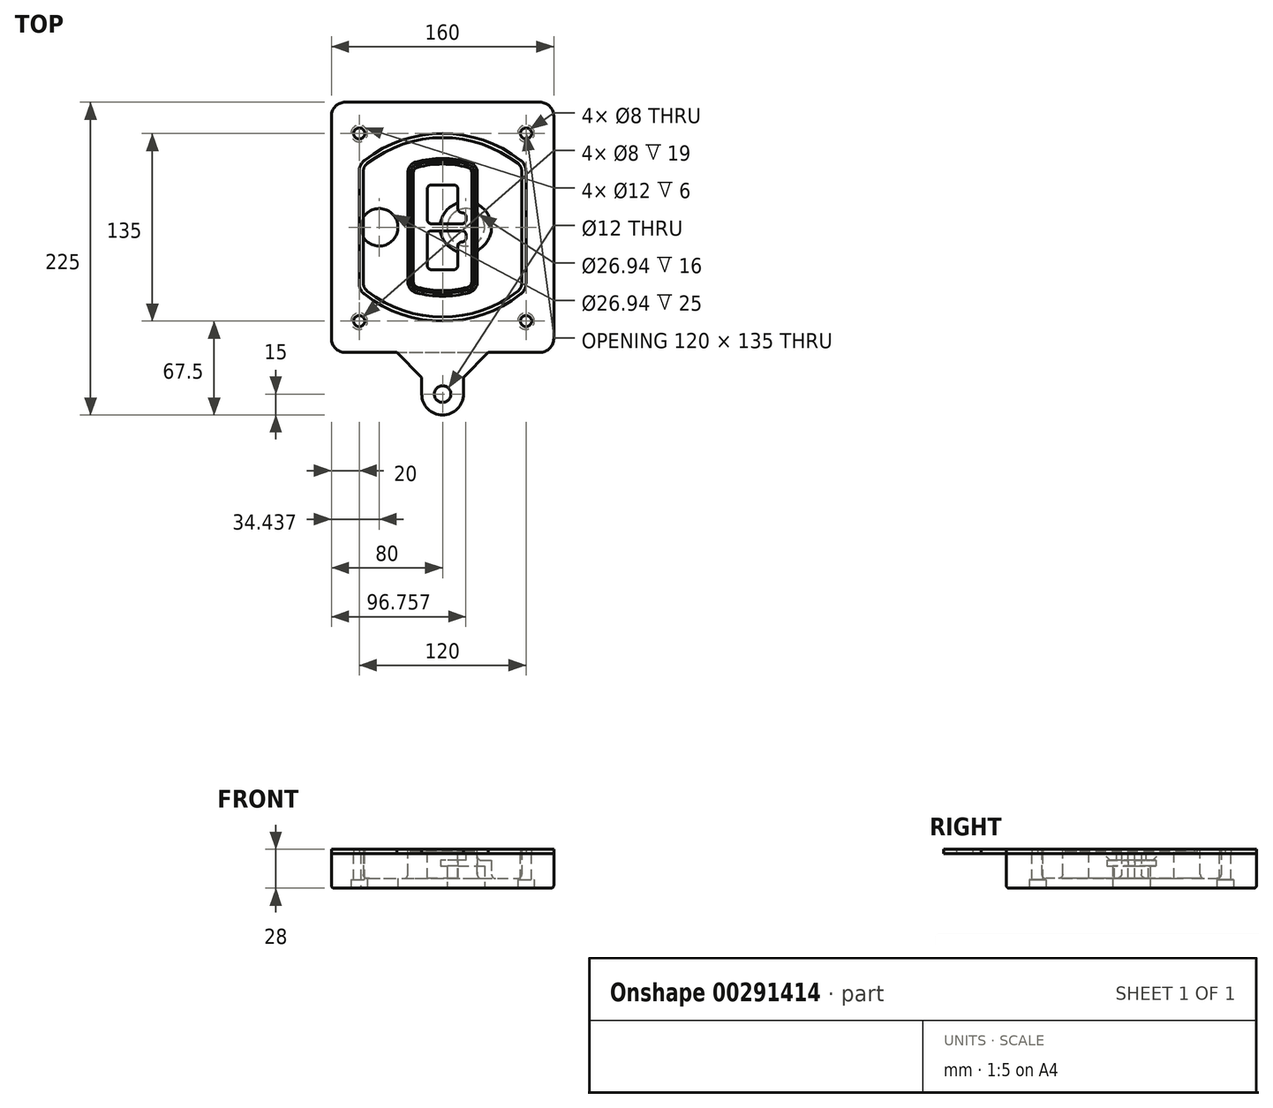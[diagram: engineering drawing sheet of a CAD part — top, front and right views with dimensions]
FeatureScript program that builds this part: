
annotation { "Feature Type Name" : "Feature", "Feature Type Description" : "" }
export const myFeature = defineFeature(function(context is Context, id is Id, definition is map)
    precondition{}
    {
        {
            var Q0;
            Q0=qCreatedBy(makeId("Top.planeOp"),FACE);
            var sketch = newSketch(context, id + "F0", { "sketchPlane" : qUnion([Q0])});
            skPoint(sketch, "E0.rect.middle", {"position": v(0, 0) * mm});
            skLineSegment(sketch, "E1.bottom", {"start": v(-70, -90) * mm, "end": v(70, -90) * mm});
            skLineSegment(sketch, "E1.top", {"start": v(-70, 90) * mm, "end": v(70, 90) * mm});
            skLineSegment(sketch, "E1.left", {"start": v(-80, -80) * mm, "end": v(-80, 80) * mm});
            skLineSegment(sketch, "E1.right", {"start": v(80, -80) * mm, "end": v(80, 80) * mm});
            skLineSegment(sketch, "E2", {"start": v(-80, 90) * mm, "end": v(80, -90) * mm, "construction": true});
            skLineSegment(sketch, "E3", {"start": v(80, 90) * mm, "end": v(-80, -90) * mm, "construction": true});
            skCircle(sketch, "E4", {"center": v(-60, 67.5) * mm, "radius": 4 * mm});
            skCircle(sketch, "E5", {"center": v(60, 67.5) * mm, "radius": 4 * mm});
            skCircle(sketch, "E6", {"center": v(60, -67.5) * mm, "radius": 4 * mm});
            skCircle(sketch, "E7", {"center": v(-60, -67.5) * mm, "radius": 4 * mm});
            skLineSegment(sketch, "E8", {"start": v(-60, 67.5) * mm, "end": v(60, 67.5) * mm, "construction": true});
            skLineSegment(sketch, "E9", {"start": v(60, 67.5) * mm, "end": v(60, -67.5) * mm, "construction": true});
            skLineSegment(sketch, "E10", {"start": v(60, -67.5) * mm, "end": v(-60, -67.5) * mm, "construction": true});
            skLineSegment(sketch, "E11", {"start": v(-60, -67.5) * mm, "end": v(-60, 67.5) * mm, "construction": true});
            skLineSegment(sketch, "E12", {"start": v(-60, 40.3) * mm, "end": v(-60, -40.3) * mm});
            skLineSegment(sketch, "E13", {"start": v(60, 40.3) * mm, "end": v(60, -40.3) * mm});
            skArc(sketch, "E14", {"start": v(56.15, 48.18) * mm, "mid": v(0, 67.5) * mm, "end": v(-56.15, 48.18) * mm});
            skArc(sketch, "E15", {"start": v(-56.15, -48.18) * mm, "mid": v(0, -67.5) * mm, "end": v(56.15, -48.18) * mm});
            skLineSegment(sketch, "E16", {"start": v(-60, 0) * mm, "end": v(60, 0) * mm, "construction": true});
            skPoint(sketch, "E17.visualSharp", {"position": v(-60, -45) * mm});
            skArc(sketch, "E17.filletArc", {"start": v(-60, -40.3) * mm, "mid": v(-58.99, -44.68) * mm, "end": v(-56.15, -48.18) * mm});
            skPoint(sketch, "E18.visualSharp", {"position": v(-60, 45) * mm});
            skArc(sketch, "E18.filletArc", {"start": v(-56.15, 48.18) * mm, "mid": v(-58.99, 44.68) * mm, "end": v(-60, 40.3) * mm});
            skPoint(sketch, "E19.visualSharp", {"position": v(60, 45) * mm});
            skArc(sketch, "E19.filletArc", {"start": v(60, 40.3) * mm, "mid": v(58.99, 44.68) * mm, "end": v(56.15, 48.18) * mm});
            skPoint(sketch, "E20.visualSharp", {"position": v(60, -45) * mm});
            skArc(sketch, "E20.filletArc", {"start": v(56.15, -48.18) * mm, "mid": v(58.99, -44.68) * mm, "end": v(60, -40.3) * mm});
            skPoint(sketch, "E21.visualSharp", {"position": v(-80, 90) * mm});
            skArc(sketch, "E21.filletArc", {"start": v(-70, 90) * mm, "mid": v(-77.07, 87.07) * mm, "end": v(-80, 80) * mm});
            skPoint(sketch, "E22.visualSharp", {"position": v(80, 90) * mm});
            skArc(sketch, "E22.filletArc", {"start": v(80, 80) * mm, "mid": v(77.07, 87.07) * mm, "end": v(70, 90) * mm});
            skPoint(sketch, "E23.visualSharp", {"position": v(80, -90) * mm});
            skArc(sketch, "E23.filletArc", {"start": v(70, -90) * mm, "mid": v(77.07, -87.07) * mm, "end": v(80, -80) * mm});
            skPoint(sketch, "E24.visualSharp", {"position": v(-80, -90) * mm});
            skArc(sketch, "E24.filletArc", {"start": v(-80, -80) * mm, "mid": v(-77.07, -87.07) * mm, "end": v(-70, -90) * mm});
            skArc(sketch, "E25.0", {"start": v(57, 40.3) * mm, "mid": v(56.3, 43.36) * mm, "end": v(54.3, 45.81) * mm});
            skLineSegment(sketch, "E25.1", {"start": v(57, 40.3) * mm, "end": v(57, -40.3) * mm});
            skArc(sketch, "E25.2", {"start": v(54.3, -45.81) * mm, "mid": v(56.3, -43.36) * mm, "end": v(57, -40.3) * mm});
            skArc(sketch, "E25.3", {"start": v(-54.3, -45.81) * mm, "mid": v(0, -64.5) * mm, "end": v(54.3, -45.81) * mm});
            skArc(sketch, "E25.4", {"start": v(-57, -40.3) * mm, "mid": v(-56.3, -43.36) * mm, "end": v(-54.3, -45.81) * mm});
            skArc(sketch, "E25.5", {"start": v(54.3, 45.81) * mm, "mid": v(0, 64.5) * mm, "end": v(-54.3, 45.81) * mm});
            skLineSegment(sketch, "E25.6", {"start": v(-57, 40.3) * mm, "end": v(-57, -40.3) * mm});
            skArc(sketch, "E25.7", {"start": v(-54.3, 45.81) * mm, "mid": v(-56.3, 43.36) * mm, "end": v(-57, 40.3) * mm});
            skArc(sketch, "E26.0", {"start": v(-58.62, 51.33) * mm, "mid": v(-62.58, 46.43) * mm, "end": v(-64, 40.3) * mm});
            skArc(sketch, "E26.1", {"start": v(58.62, 51.33) * mm, "mid": v(0, 71.5) * mm, "end": v(-58.62, 51.33) * mm});
            skArc(sketch, "E26.2", {"start": v(64, 40.3) * mm, "mid": v(62.58, 46.43) * mm, "end": v(58.62, 51.33) * mm});
            skLineSegment(sketch, "E26.3", {"start": v(64, 40.3) * mm, "end": v(64, -40.3) * mm});
            skArc(sketch, "E26.4", {"start": v(58.62, -51.33) * mm, "mid": v(62.58, -46.43) * mm, "end": v(64, -40.3) * mm});
            skLineSegment(sketch, "E26.5", {"start": v(-64, 40.3) * mm, "end": v(-64, -40.3) * mm});
            skArc(sketch, "E26.6", {"start": v(-58.62, -51.33) * mm, "mid": v(0, -71.5) * mm, "end": v(58.62, -51.33) * mm});
            skArc(sketch, "E26.7", {"start": v(-64, -40.3) * mm, "mid": v(-62.58, -46.43) * mm, "end": v(-58.62, -51.33) * mm});
            skSolve(sketch);
        }
        {
            var Q0;
            Q0=makeQuery(id+"F0.imprint","IMPRINT",FACE,{"disambiguationData":[TD([[makeQuery(id+"F0.imprint","IMPRINT",EDGE,{"derivedFrom":sQuery(id+"F0.wireOp",EDGE,"E1.bottom")}),1.0]])]});
            var Q1;
            Q1=makeQuery(id+"F0.imprint","IMPRINT",FACE,{"disambiguationData":[TD([[makeQuery(id+"F0.imprint","IMPRINT",EDGE,{"derivedFrom":sQuery(id+"F0.wireOp",EDGE,"E12")}),1.0]])]});
            var Q2;
            Q2=makeQuery(id+"F0.imprint","IMPRINT",FACE,{"disambiguationData":[TD([[makeQuery(id+"F0.imprint","IMPRINT",EDGE,{"derivedFrom":sQuery(id+"F0.wireOp",EDGE,"E25.0")}),1.0]])]});
            var Q3;
            Q3=makeQuery(id+"F0.imprint","IMPRINT",FACE,{"disambiguationData":[TD([[makeQuery(id+"F0.imprint","IMPRINT",EDGE,{"derivedFrom":sQuery(id+"F0.wireOp",EDGE,"E12")}),-1.0]])]});
            extrude(context, id + "F1", {"entities" : qUnion([Q0, Q1, Q2, Q3]), "oppositeDirection" : true, "depth" : 25 * mm});
        }
        {
            var Q0;
            Q0=makeQuery(id+"F0.imprint","IMPRINT",FACE,{"disambiguationData":[TD([[makeQuery(id+"F0.imprint","IMPRINT",EDGE,{"derivedFrom":sQuery(id+"F0.wireOp",EDGE,"E12")}),1.0]])]});
            extrude(context, id + "F2", {"entities" : qUnion([Q0]), "operationType" : NewBodyOperationType.ADD, "depth" : 3 * mm});
        }
        {
            var Q0;
            Q0=makeQuery(id+"F0.imprint","IMPRINT",FACE,{"disambiguationData":[TD([[makeQuery(id+"F0.imprint","IMPRINT",EDGE,{"derivedFrom":sQuery(id+"F0.wireOp",EDGE,"E25.0")}),1.0]])]});
            extrude(context, id + "F3", {"entities" : qUnion([Q0]), "operationType" : NewBodyOperationType.REMOVE, "oppositeDirection" : true, "depth" : 18 * mm});
        }
        {
            var Q0;
            Q0=makeQuery(id+"F2.opExtrude","CAP_FACE",FACE,{"disambiguationData":[OSD([sQuery(id+"F0.wireOp",EDGE,"E12"),sQuery(id+"F0.wireOp",EDGE,"E13"),sQuery(id+"F0.wireOp",EDGE,"E14"),sQuery(id+"F0.wireOp",EDGE,"E15"),sQuery(id+"F0.wireOp",EDGE,"E17.filletArc"),sQuery(id+"F0.wireOp",EDGE,"E18.filletArc"),sQuery(id+"F0.wireOp",EDGE,"E19.filletArc"),sQuery(id+"F0.wireOp",EDGE,"E20.filletArc"),sQuery(id+"F0.wireOp",EDGE,"E25.0"),sQuery(id+"F0.wireOp",EDGE,"E25.1"),sQuery(id+"F0.wireOp",EDGE,"E25.2"),sQuery(id+"F0.wireOp",EDGE,"E25.3"),sQuery(id+"F0.wireOp",EDGE,"E25.4"),sQuery(id+"F0.wireOp",EDGE,"E25.5"),sQuery(id+"F0.wireOp",EDGE,"E25.6"),sQuery(id+"F0.wireOp",EDGE,"E25.7")])],"isStart":false});
            var sketch = newSketch(context, id + "F4", { "sketchPlane" : qUnion([Q0])});
            skArc(sketch, "E27.0", {"start": v(-19.08, -46.97) * mm, "mid": v(0, -49.5) * mm, "end": v(19.08, -46.97) * mm});
            skArc(sketch, "E28.0", {"start": v(19.08, 46.97) * mm, "mid": v(0, 49.5) * mm, "end": v(-19.08, 46.97) * mm});
            skLineSegment(sketch, "E29", {"start": v(-25, 39.25) * mm, "end": v(-25, -39.25) * mm});
            skLineSegment(sketch, "E30", {"start": v(25, 39.25) * mm, "end": v(25, -39.25) * mm});
            skLineSegment(sketch, "E31", {"start": v(-25, 45.1) * mm, "end": v(25, 45.1) * mm, "construction": true});
            skLineSegment(sketch, "E32", {"start": v(-25, -45.1) * mm, "end": v(25, -45.1) * mm, "construction": true});
            skPoint(sketch, "E33.visualSharp", {"position": v(-25, 45.1) * mm});
            skArc(sketch, "E33.filletArc", {"start": v(-19.08, 46.97) * mm, "mid": v(-23.35, 44.11) * mm, "end": v(-25, 39.25) * mm});
            skPoint(sketch, "E34.visualSharp", {"position": v(25, 45.1) * mm});
            skArc(sketch, "E34.filletArc", {"start": v(25, 39.25) * mm, "mid": v(23.35, 44.11) * mm, "end": v(19.08, 46.97) * mm});
            skPoint(sketch, "E35.visualSharp", {"position": v(25, -45.1) * mm});
            skArc(sketch, "E35.filletArc", {"start": v(19.08, -46.97) * mm, "mid": v(23.35, -44.11) * mm, "end": v(25, -39.25) * mm});
            skPoint(sketch, "E36.visualSharp", {"position": v(-25, -45.1) * mm});
            skArc(sketch, "E36.filletArc", {"start": v(-25, -39.25) * mm, "mid": v(-23.35, -44.11) * mm, "end": v(-19.08, -46.97) * mm});
            skArc(sketch, "E37.0", {"start": v(54.3, 45.81) * mm, "mid": v(0, 64.5) * mm, "end": v(-54.3, 45.81) * mm});
            skArc(sketch, "E37.1", {"start": v(-54.3, 45.81) * mm, "mid": v(-56.3, 43.36) * mm, "end": v(-57, 40.3) * mm});
            skLineSegment(sketch, "E37.2", {"start": v(-57, 40.3) * mm, "end": v(-57, -40.3) * mm});
            skArc(sketch, "E37.3", {"start": v(-57, -40.3) * mm, "mid": v(-56.3, -43.36) * mm, "end": v(-54.3, -45.81) * mm});
            skArc(sketch, "E37.4", {"start": v(-54.3, -45.81) * mm, "mid": v(0, -64.5) * mm, "end": v(54.3, -45.81) * mm});
            skArc(sketch, "E37.5", {"start": v(54.3, -45.81) * mm, "mid": v(56.3, -43.36) * mm, "end": v(57, -40.3) * mm});
            skLineSegment(sketch, "E37.6", {"start": v(57, 40.3) * mm, "end": v(57, -40.3) * mm});
            skArc(sketch, "E37.7", {"start": v(57, 40.3) * mm, "mid": v(56.3, 43.36) * mm, "end": v(54.3, 45.81) * mm});
            skLineSegment(sketch, "E38.0", {"start": v(23, 39.25) * mm, "end": v(23, -39.25) * mm});
            skArc(sketch, "E38.1", {"start": v(18.56, -45.04) * mm, "mid": v(21.76, -42.9) * mm, "end": v(23, -39.25) * mm});
            skArc(sketch, "E38.2", {"start": v(-18.56, -45.04) * mm, "mid": v(0, -47.5) * mm, "end": v(18.56, -45.04) * mm});
            skArc(sketch, "E38.3", {"start": v(-23, -39.25) * mm, "mid": v(-21.76, -42.9) * mm, "end": v(-18.56, -45.04) * mm});
            skLineSegment(sketch, "E38.4", {"start": v(-23, 39.25) * mm, "end": v(-23, -39.25) * mm});
            skArc(sketch, "E38.5", {"start": v(23, 39.25) * mm, "mid": v(21.76, 42.9) * mm, "end": v(18.56, 45.04) * mm});
            skArc(sketch, "E38.6", {"start": v(-18.56, 45.04) * mm, "mid": v(-21.76, 42.9) * mm, "end": v(-23, 39.25) * mm});
            skArc(sketch, "E38.7", {"start": v(18.56, 45.04) * mm, "mid": v(0, 47.5) * mm, "end": v(-18.56, 45.04) * mm});
            skArc(sketch, "E39.0", {"start": v(21, 39.25) * mm, "mid": v(20.18, 41.68) * mm, "end": v(18.04, 43.1) * mm});
            skLineSegment(sketch, "E39.1", {"start": v(21, 39.25) * mm, "end": v(21, -39.25) * mm});
            skArc(sketch, "E39.2", {"start": v(18.04, -43.1) * mm, "mid": v(20.18, -41.68) * mm, "end": v(21, -39.25) * mm});
            skArc(sketch, "E39.3", {"start": v(-18.04, -43.1) * mm, "mid": v(0, -45.5) * mm, "end": v(18.04, -43.1) * mm});
            skArc(sketch, "E39.4", {"start": v(-21, -39.25) * mm, "mid": v(-20.18, -41.68) * mm, "end": v(-18.04, -43.1) * mm});
            skArc(sketch, "E39.5", {"start": v(18.04, 43.1) * mm, "mid": v(0, 45.5) * mm, "end": v(-18.04, 43.1) * mm});
            skLineSegment(sketch, "E39.6", {"start": v(-21, 39.25) * mm, "end": v(-21, -39.25) * mm});
            skArc(sketch, "E39.7", {"start": v(-18.04, 43.1) * mm, "mid": v(-20.18, 41.68) * mm, "end": v(-21, 39.25) * mm});
            skLineSegment(sketch, "E40", {"start": v(-25, 0) * mm, "end": v(25, 0) * mm, "construction": true});
            skLineSegment(sketch, "E41", {"start": v(-11, 5.5) * mm, "end": v(-11, 27.5) * mm});
            skLineSegment(sketch, "E42", {"start": v(-8, 30.5) * mm, "end": v(8, 30.5) * mm});
            skLineSegment(sketch, "E43", {"start": v(11, 27.5) * mm, "end": v(11, 13.5) * mm});
            skLineSegment(sketch, "E44", {"start": v(14, 10.5) * mm, "end": v(14, 10.5) * mm});
            skLineSegment(sketch, "E45", {"start": v(17, 7.5) * mm, "end": v(17, 5.5) * mm});
            skLineSegment(sketch, "E46", {"start": v(14, 2.5) * mm, "end": v(-8, 2.5) * mm});
            skPoint(sketch, "E47.visualSharp", {"position": v(-11, 30.5) * mm});
            skArc(sketch, "E47.filletArc", {"start": v(-8, 30.5) * mm, "mid": v(-10.12, 29.62) * mm, "end": v(-11, 27.5) * mm});
            skPoint(sketch, "E48.visualSharp", {"position": v(11, 30.5) * mm});
            skArc(sketch, "E48.filletArc", {"start": v(11, 27.5) * mm, "mid": v(10.12, 29.62) * mm, "end": v(8, 30.5) * mm});
            skPoint(sketch, "E49.visualSharp", {"position": v(11, 10.5) * mm});
            skArc(sketch, "E49.filletArc", {"start": v(11, 13.5) * mm, "mid": v(11.88, 11.38) * mm, "end": v(14, 10.5) * mm});
            skPoint(sketch, "E50.visualSharp", {"position": v(17, 10.5) * mm});
            skArc(sketch, "E50.filletArc", {"start": v(17, 7.5) * mm, "mid": v(16.12, 9.62) * mm, "end": v(14, 10.5) * mm});
            skPoint(sketch, "E51.visualSharp", {"position": v(17, 2.5) * mm});
            skArc(sketch, "E51.filletArc", {"start": v(14, 2.5) * mm, "mid": v(16.12, 3.38) * mm, "end": v(17, 5.5) * mm});
            skPoint(sketch, "E52.visualSharp", {"position": v(-11, 2.5) * mm});
            skArc(sketch, "E52.filletArc", {"start": v(-11, 5.5) * mm, "mid": v(-10.12, 3.38) * mm, "end": v(-8, 2.5) * mm});
            skLineSegment(sketch, "E53.0.MirrorCS", {"start": v(14, -2.5) * mm, "end": v(-8, -2.5) * mm});
            skArc(sketch, "E54.0.MirrorCS", {"start": v(-11, -5.5) * mm, "mid": v(-10.12, -3.38) * mm, "end": v(-8, -2.5) * mm});
            skLineSegment(sketch, "E55.0.MirrorCS", {"start": v(-11, -5.5) * mm, "end": v(-11, -27.5) * mm});
            skArc(sketch, "E56.0.MirrorCS", {"start": v(-8, -30.5) * mm, "mid": v(-10.12, -29.62) * mm, "end": v(-11, -27.5) * mm});
            skLineSegment(sketch, "E57.0.MirrorCS", {"start": v(-8, -30.5) * mm, "end": v(8, -30.5) * mm});
            skArc(sketch, "E58.0.MirrorCS", {"start": v(11, -27.5) * mm, "mid": v(10.12, -29.62) * mm, "end": v(8, -30.5) * mm});
            skLineSegment(sketch, "E59.0.MirrorCS", {"start": v(11, -27.5) * mm, "end": v(11, -13.5) * mm});
            skArc(sketch, "E60.0.MirrorCS", {"start": v(11, -13.5) * mm, "mid": v(11.88, -11.38) * mm, "end": v(14, -10.5) * mm});
            skArc(sketch, "E61.0.MirrorCS", {"start": v(17, -7.5) * mm, "mid": v(16.12, -9.62) * mm, "end": v(14, -10.5) * mm});
            skLineSegment(sketch, "E62.0.MirrorCS", {"start": v(17, -7.5) * mm, "end": v(17, -5.5) * mm});
            skArc(sketch, "E63.0.MirrorCS", {"start": v(14, -2.5) * mm, "mid": v(16.12, -3.38) * mm, "end": v(17, -5.5) * mm});
            skSolve(sketch);
        }
        {
            var Q0;
            Q0=makeQuery(id+"F4.imprint","IMPRINT",FACE,{"disambiguationData":[TD([[makeQuery(id+"F4.imprint","IMPRINT",EDGE,{"derivedFrom":sQuery(id+"F4.wireOp",EDGE,"E27.0")}),1.0]])]});
            var Q1;
            Q1=makeQuery(id+"F4.imprint","IMPRINT",FACE,{"disambiguationData":[TD([[makeQuery(id+"F4.imprint","IMPRINT",EDGE,{"derivedFrom":sQuery(id+"F4.wireOp",EDGE,"E38.0")}),-1.0]])]});
            var Q2;
            Q2=makeQuery(id+"F4.imprint","IMPRINT",FACE,{"disambiguationData":[TD([[makeQuery(id+"F4.imprint","IMPRINT",EDGE,{"derivedFrom":sQuery(id+"F4.wireOp",EDGE,"E39.0")}),1.0]])]});
            extrude(context, id + "F5", {"entities" : qUnion([Q0, Q1, Q2]), "operationType" : NewBodyOperationType.ADD, "endBound" : BoundingType.UP_TO_NEXT, "oppositeDirection" : true, "depth" : 25 * mm});
        }
        {
            var Q0;
            Q0=makeQuery(id+"F4.imprint","IMPRINT",FACE,{"disambiguationData":[TD([[makeQuery(id+"F4.imprint","IMPRINT",EDGE,{"derivedFrom":sQuery(id+"F4.wireOp",EDGE,"E38.0")}),-1.0]])]});
            extrude(context, id + "F6", {"entities" : qUnion([Q0]), "operationType" : NewBodyOperationType.REMOVE, "oppositeDirection" : true, "depth" : 2 * mm});
        }
        {
            var Q0;
            Q0=makeQuery(id+"F1.opExtrude","CAP_FACE",FACE,{"disambiguationData":[OSD([sQuery(id+"F0.wireOp",EDGE,"E1.bottom"),sQuery(id+"F0.wireOp",EDGE,"E1.top"),sQuery(id+"F0.wireOp",EDGE,"E1.left"),sQuery(id+"F0.wireOp",EDGE,"E1.right"),sQuery(id+"F0.wireOp",EDGE,"E4"),sQuery(id+"F0.wireOp",EDGE,"E5"),sQuery(id+"F0.wireOp",EDGE,"E6"),sQuery(id+"F0.wireOp",EDGE,"E7"),sQuery(id+"F0.wireOp",EDGE,"E21.filletArc"),sQuery(id+"F0.wireOp",EDGE,"E22.filletArc"),sQuery(id+"F0.wireOp",EDGE,"E23.filletArc"),sQuery(id+"F0.wireOp",EDGE,"E24.filletArc")])],"isStart":false});
            var sketch = newSketch(context, id + "F7", { "sketchPlane" : qUnion([Q0])});
            skCircle(sketch, "E64", {"center": v(16.76, 0) * mm, "radius": 13.47 * mm});
            skCircle(sketch, "E65", {"center": v(-45.56, 0) * mm, "radius": 13.47 * mm});
            skLineSegment(sketch, "E66", {"start": v(80, 0) * mm, "end": v(-80, 0) * mm});
            skCircle(sketch, "E67", {"center": v(16.76, 0) * mm, "radius": 18.47 * mm});
            skCircle(sketch, "E68", {"center": v(60, -67.5) * mm, "radius": 6 * mm});
            skCircle(sketch, "E69", {"center": v(-60, -67.5) * mm, "radius": 6 * mm});
            skCircle(sketch, "E70", {"center": v(-60, 67.5) * mm, "radius": 6 * mm});
            skCircle(sketch, "E71", {"center": v(60, 67.5) * mm, "radius": 6 * mm});
            skSolve(sketch);
        }
        {
            var Q0;
            {var subQ1=sQuery(id+"F7.wireOp",EDGE,"E66");var subQ4=sQuery(id+"F7.wireOp",EDGE,"E64");var subQ6=makeQuery(id+"F7.imprint","INTERSECT",VERTEX,{"disambiguationData":[OD(0.0)],"derivedFrom":[subQ4,subQ1]});Q0=makeQuery(id+"F7.imprint","IMPRINT",FACE,{"disambiguationData":[TD([[makeQuery(id+"F7.imprint","IMPRINT",EDGE,{"disambiguationData":[TD([[subQ6,-1.0]])],"derivedFrom":subQ4}),-1.0]])]});}
            var Q1;
            {var subQ0=sQuery(id+"F7.wireOp",EDGE,"E66");var subQ1=sQuery(id+"F7.wireOp",EDGE,"E64");var subQ3=makeQuery(id+"F7.imprint","INTERSECT",VERTEX,{"disambiguationData":[OD(0.0)],"derivedFrom":[subQ1,subQ0]});Q1=makeQuery(id+"F7.imprint","IMPRINT",FACE,{"disambiguationData":[TD([[makeQuery(id+"F7.imprint","IMPRINT",EDGE,{"disambiguationData":[TD([[subQ3,-1.0]])],"derivedFrom":subQ1}),1.0]])]});}
            var Q2;
            {var subQ0=sQuery(id+"F7.wireOp",EDGE,"E66");var subQ1=sQuery(id+"F7.wireOp",EDGE,"E64");var subQ3=makeQuery(id+"F7.imprint","INTERSECT",VERTEX,{"disambiguationData":[OD(0.0)],"derivedFrom":[subQ1,subQ0]});Q2=makeQuery(id+"F7.imprint","IMPRINT",FACE,{"disambiguationData":[TD([[makeQuery(id+"F7.imprint","IMPRINT",EDGE,{"disambiguationData":[TD([[subQ3,1.0]])],"derivedFrom":subQ1}),1.0]])]});}
            var Q3;
            {var subQ1=sQuery(id+"F7.wireOp",EDGE,"E66");var subQ4=sQuery(id+"F7.wireOp",EDGE,"E64");var subQ6=makeQuery(id+"F7.imprint","INTERSECT",VERTEX,{"disambiguationData":[OD(0.0)],"derivedFrom":[subQ4,subQ1]});Q3=makeQuery(id+"F7.imprint","IMPRINT",FACE,{"disambiguationData":[TD([[makeQuery(id+"F7.imprint","IMPRINT",EDGE,{"disambiguationData":[TD([[subQ6,1.0]])],"derivedFrom":subQ4}),-1.0]])]});}
            extrude(context, id + "F8", {"entities" : qUnion([Q0, Q1, Q2, Q3]), "operationType" : NewBodyOperationType.ADD, "oppositeDirection" : true, "depth" : 20 * mm});
        }
        {
            var Q0;
            {var subQ0=sQuery(id+"F7.wireOp",EDGE,"E66");var subQ1=sQuery(id+"F7.wireOp",EDGE,"E64");var subQ3=makeQuery(id+"F7.imprint","INTERSECT",VERTEX,{"disambiguationData":[OD(0.0)],"derivedFrom":[subQ1,subQ0]});Q0=makeQuery(id+"F7.imprint","IMPRINT",FACE,{"disambiguationData":[TD([[makeQuery(id+"F7.imprint","IMPRINT",EDGE,{"disambiguationData":[TD([[subQ3,-1.0]])],"derivedFrom":subQ1}),1.0]])]});}
            var Q1;
            {var subQ0=sQuery(id+"F7.wireOp",EDGE,"E66");var subQ1=sQuery(id+"F7.wireOp",EDGE,"E64");var subQ3=makeQuery(id+"F7.imprint","INTERSECT",VERTEX,{"disambiguationData":[OD(0.0)],"derivedFrom":[subQ1,subQ0]});Q1=makeQuery(id+"F7.imprint","IMPRINT",FACE,{"disambiguationData":[TD([[makeQuery(id+"F7.imprint","IMPRINT",EDGE,{"disambiguationData":[TD([[subQ3,1.0]])],"derivedFrom":subQ1}),1.0]])]});}
            extrude(context, id + "F9", {"entities" : qUnion([Q0, Q1]), "operationType" : NewBodyOperationType.REMOVE, "oppositeDirection" : true, "depth" : 16 * mm});
        }
        {
            var Q0;
            {var subQ0=sQuery(id+"F7.wireOp",EDGE,"E66");var subQ1=sQuery(id+"F7.wireOp",EDGE,"E65");var subQ3=makeQuery(id+"F7.imprint","INTERSECT",VERTEX,{"disambiguationData":[OD(0.0)],"derivedFrom":[subQ1,subQ0]});Q0=makeQuery(id+"F7.imprint","IMPRINT",FACE,{"disambiguationData":[TD([[makeQuery(id+"F7.imprint","IMPRINT",EDGE,{"disambiguationData":[TD([[subQ3,-1.0]])],"derivedFrom":subQ1}),1.0]])]});}
            var Q1;
            {var subQ0=sQuery(id+"F7.wireOp",EDGE,"E66");var subQ1=sQuery(id+"F7.wireOp",EDGE,"E65");var subQ3=makeQuery(id+"F7.imprint","INTERSECT",VERTEX,{"disambiguationData":[OD(0.0)],"derivedFrom":[subQ1,subQ0]});Q1=makeQuery(id+"F7.imprint","IMPRINT",FACE,{"disambiguationData":[TD([[makeQuery(id+"F7.imprint","IMPRINT",EDGE,{"disambiguationData":[TD([[subQ3,1.0]])],"derivedFrom":subQ1}),1.0]])]});}
            extrude(context, id + "F10", {"entities" : qUnion([Q0, Q1]), "operationType" : NewBodyOperationType.REMOVE, "oppositeDirection" : true, "depth" : 25 * mm});
        }
        {
            var Q0;
            Q0=makeQuery(id+"F7.imprint","IMPRINT",FACE,{"disambiguationData":[TD([[makeQuery(id+"F7.imprint","IMPRINT",EDGE,{"derivedFrom":sQuery(id+"F7.wireOp",EDGE,"E68")}),1.0]])]});
            var Q1;
            Q1=makeQuery(id+"F7.imprint","IMPRINT",FACE,{"disambiguationData":[TD([[makeQuery(id+"F7.imprint","IMPRINT",EDGE,{"derivedFrom":makeQuery(id+"F1.opExtrude","CAP_EDGE",EDGE,{"disambiguationData":[OSD([sQuery(id+"F0.wireOp",EDGE,"E5")])],"isStart":false})}),-1.0]])]});
            var Q2;
            Q2=makeQuery(id+"F7.imprint","IMPRINT",FACE,{"disambiguationData":[TD([[makeQuery(id+"F7.imprint","IMPRINT",EDGE,{"derivedFrom":sQuery(id+"F7.wireOp",EDGE,"E69")}),1.0]])]});
            var Q3;
            Q3=makeQuery(id+"F7.imprint","IMPRINT",FACE,{"disambiguationData":[TD([[makeQuery(id+"F7.imprint","IMPRINT",EDGE,{"derivedFrom":makeQuery(id+"F1.opExtrude","CAP_EDGE",EDGE,{"disambiguationData":[OSD([sQuery(id+"F0.wireOp",EDGE,"E4")])],"isStart":false})}),-1.0]])]});
            var Q4;
            Q4=makeQuery(id+"F7.imprint","IMPRINT",FACE,{"disambiguationData":[TD([[makeQuery(id+"F7.imprint","IMPRINT",EDGE,{"derivedFrom":sQuery(id+"F7.wireOp",EDGE,"E70")}),1.0]])]});
            var Q5;
            Q5=makeQuery(id+"F7.imprint","IMPRINT",FACE,{"disambiguationData":[TD([[makeQuery(id+"F7.imprint","IMPRINT",EDGE,{"derivedFrom":makeQuery(id+"F1.opExtrude","CAP_EDGE",EDGE,{"disambiguationData":[OSD([sQuery(id+"F0.wireOp",EDGE,"E7")])],"isStart":false})}),-1.0]])]});
            var Q6;
            Q6=makeQuery(id+"F7.imprint","IMPRINT",FACE,{"disambiguationData":[TD([[makeQuery(id+"F7.imprint","IMPRINT",EDGE,{"derivedFrom":sQuery(id+"F7.wireOp",EDGE,"E71")}),1.0]])]});
            var Q7;
            Q7=makeQuery(id+"F7.imprint","IMPRINT",FACE,{"disambiguationData":[TD([[makeQuery(id+"F7.imprint","IMPRINT",EDGE,{"derivedFrom":makeQuery(id+"F1.opExtrude","CAP_EDGE",EDGE,{"disambiguationData":[OSD([sQuery(id+"F0.wireOp",EDGE,"E6")])],"isStart":false})}),-1.0]])]});
            extrude(context, id + "F11", {"entities" : qUnion([Q0, Q1, Q2, Q3, Q4, Q5, Q6, Q7]), "operationType" : NewBodyOperationType.REMOVE, "oppositeDirection" : true, "depth" : 6 * mm});
        }
        {
            var Q0;
            Q0=makeQuery(id+"F9.boolean.opBoolean","COPY",FACE,{"derivedFrom":makeQuery(id+"F9.opExtrude","CAP_FACE",FACE,{"disambiguationData":[OSD([sQuery(id+"F7.wireOp",EDGE,"E64")])],"isStart":false})});
            var sketch = newSketch(context, id + "F12", { "sketchPlane" : qUnion([Q0])});
            skArc(sketch, "E72.0", {"start": v(11, 17.55) * mm, "mid": v(2.57, 11.82) * mm, "end": v(-1.54, 2.5) * mm});
            skArc(sketch, "E72.1", {"start": v(-1.54, -2.5) * mm, "mid": v(2.57, -11.82) * mm, "end": v(11, -17.55) * mm});
            skLineSegment(sketch, "E73", {"start": v(-1.54, -2.5) * mm, "end": v(14, -2.5) * mm});
            skLineSegment(sketch, "E74.0", {"start": v(14, 2.5) * mm, "end": v(-1.54, 2.5) * mm});
            skArc(sketch, "E74.1", {"start": v(14, 2.5) * mm, "mid": v(16.12, 3.38) * mm, "end": v(17, 5.5) * mm});
            skLineSegment(sketch, "E74.2", {"start": v(17, 7.5) * mm, "end": v(17, 5.5) * mm});
            skArc(sketch, "E74.3", {"start": v(17, 7.5) * mm, "mid": v(16.12, 9.62) * mm, "end": v(14, 10.5) * mm});
            skArc(sketch, "E74.4", {"start": v(11, 13.5) * mm, "mid": v(11.88, 11.38) * mm, "end": v(14, 10.5) * mm});
            skLineSegment(sketch, "E74.5", {"start": v(11, 17.55) * mm, "end": v(11, 13.5) * mm});
            skLineSegment(sketch, "E74.7", {"start": v(14, -2.5) * mm, "end": v(-1.54, -2.5) * mm});
            skArc(sketch, "E74.8", {"start": v(14, -2.5) * mm, "mid": v(16.12, -3.38) * mm, "end": v(17, -5.5) * mm});
            skLineSegment(sketch, "E74.9", {"start": v(17, -7.5) * mm, "end": v(17, -5.5) * mm});
            skArc(sketch, "E74.10", {"start": v(17, -7.5) * mm, "mid": v(16.12, -9.62) * mm, "end": v(14, -10.5) * mm});
            skArc(sketch, "E74.11", {"start": v(11, -13.5) * mm, "mid": v(11.88, -11.38) * mm, "end": v(14, -10.5) * mm});
            skLineSegment(sketch, "E74.12", {"start": v(11, -17.55) * mm, "end": v(11, -13.5) * mm});
            skPoint(sketch, "E75.orphan", {"position": v(11, -27.5) * mm});
            skPoint(sketch, "E76.orphan", {"position": v(-8, -2.5) * mm});
            skPoint(sketch, "E77.orphan", {"position": v(-8, 2.5) * mm});
            skPoint(sketch, "E78.orphan", {"position": v(11, 27.5) * mm});
            skSolve(sketch);
        }
        {
            var Q0;
            {var subQ7=sQuery(id+"F12.wireOp",EDGE,"E72.0");var subQ14=sQuery(id+"F12.wireOp",EDGE,"E72.1");var subQ16=sQuery(id+"F12.wireOp",EDGE,"E74.1");var subQ18=sQuery(id+"F12.wireOp",EDGE,"E74.8");Q0=qUnion([makeQuery(id+"F12.imprint","IMPRINT",FACE,{"disambiguationData":[TD([[makeQuery(id+"F12.imprint","IMPRINT",EDGE,{"derivedFrom":subQ7}),1.0]])]}),makeQuery(id+"F12.imprint","IMPRINT",FACE,{"disambiguationData":[TD([[makeQuery(id+"F12.imprint","IMPRINT",EDGE,{"derivedFrom":subQ14}),1.0]])]}),makeQuery(id+"F12.imprint","IMPRINT",FACE,{"disambiguationData":[TD([[makeQuery(id+"F12.imprint","IMPRINT",EDGE,{"derivedFrom":subQ16}),1.0]])]}),makeQuery(id+"F12.imprint","IMPRINT",FACE,{"disambiguationData":[TD([[makeQuery(id+"F12.imprint","IMPRINT",EDGE,{"derivedFrom":subQ18}),-1.0]])]})]);}
            var Q1;
            Q1=makeQuery(id+"F5.boolean.opBoolean","SPLIT",FACE,{"disambiguationData":[TD([makeQuery(id+"F5.opExtrude","SWEPT_FACE",FACE,{"disambiguationData":[OSD([sQuery(id+"F4.wireOp",EDGE,"E41")])]})])],"derivedFrom":makeQuery(id+"F3.boolean.opBoolean","COPY",FACE,{"derivedFrom":makeQuery(id+"F3.opExtrude","CAP_FACE",FACE,{"disambiguationData":[OSD([sQuery(id+"F0.wireOp",EDGE,"E25.0"),sQuery(id+"F0.wireOp",EDGE,"E25.1"),sQuery(id+"F0.wireOp",EDGE,"E25.2"),sQuery(id+"F0.wireOp",EDGE,"E25.3"),sQuery(id+"F0.wireOp",EDGE,"E25.4"),sQuery(id+"F0.wireOp",EDGE,"E25.5"),sQuery(id+"F0.wireOp",EDGE,"E25.6"),sQuery(id+"F0.wireOp",EDGE,"E25.7")])],"isStart":false})})});
            extrude(context, id + "F13", {"entities" : qUnion([Q0]), "operationType" : NewBodyOperationType.REMOVE, "endBound" : BoundingType.UP_TO_SURFACE, "endBoundEntityFace" : qUnion([Q1]), "depth" : 25 * mm});
        }
        {
            var Q0;
            Q0=makeQuery(id+"F3.boolean.opBoolean","COPY",EDGE,{"derivedFrom":makeQuery(id+"F3.opExtrude","CAP_EDGE",EDGE,{"disambiguationData":[OSD([sQuery(id+"F0.wireOp",EDGE,"E25.6")])],"isStart":false})});
            var Q1;
            Q1=makeQuery(id+"F8.boolean.opBoolean","INTERSECT",EDGE,{"derivedFrom":[makeQuery(id+"F5.opExtrude","SWEPT_FACE",FACE,{"disambiguationData":[OSD([sQuery(id+"F4.wireOp",EDGE,"E30")])]}),makeQuery(id+"F8.opExtrude","CAP_FACE",FACE,{"disambiguationData":[OSD([sQuery(id+"F7.wireOp",EDGE,"E67")])],"isStart":false})]});
            var Q2;
            Q2=makeQuery(id+"F8.boolean.opBoolean","INTERSECT",EDGE,{"disambiguationData":[OD(1.0)],"derivedFrom":[makeQuery(id+"F5.opExtrude","SWEPT_FACE",FACE,{"disambiguationData":[OSD([sQuery(id+"F4.wireOp",EDGE,"E30")])]}),makeQuery(id+"F8.opExtrude","SWEPT_FACE",FACE,{"disambiguationData":[OSD([sQuery(id+"F7.wireOp",EDGE,"E67")])]})]});
            var Q3;
            {var subQ0=sQuery(id+"F4.wireOp",EDGE,"E30");Q3=makeQuery(id+"F8.boolean.opBoolean","SPLIT",EDGE,{"disambiguationData":[TD([makeQuery(id+"F5.opExtrude","SWEPT_FACE",FACE,{"disambiguationData":[OSD([sQuery(id+"F4.wireOp",EDGE,"E35.filletArc")])]})])],"derivedFrom":makeQuery(id+"F5.opExtrude","CAP_EDGE",EDGE,{"disambiguationData":[OSD([subQ0])],"isStart":false})});}
            var Q4;
            {var subQ0=sQuery(id+"F0.wireOp",EDGE,"E25.7");var subQ1=sQuery(id+"F0.wireOp",EDGE,"E25.1");var subQ2=sQuery(id+"F0.wireOp",EDGE,"E25.6");var subQ3=sQuery(id+"F0.wireOp",EDGE,"E25.5");var subQ4=sQuery(id+"F0.wireOp",EDGE,"E25.4");var subQ5=sQuery(id+"F0.wireOp",EDGE,"E25.0");var subQ6=sQuery(id+"F0.wireOp",EDGE,"E25.2");var subQ7=sQuery(id+"F0.wireOp",EDGE,"E25.3");Q4=makeQuery(id+"F8.boolean.opBoolean","INTERSECT",EDGE,{"derivedFrom":[makeQuery(id+"F5.boolean.opBoolean","SPLIT",FACE,{"disambiguationData":[TD([makeQuery(id+"F2.opExtrude","SWEPT_FACE",FACE,{"disambiguationData":[OSD([subQ5])]})])],"derivedFrom":makeQuery(id+"F3.boolean.opBoolean","COPY",FACE,{"derivedFrom":makeQuery(id+"F3.opExtrude","CAP_FACE",FACE,{"disambiguationData":[OSD([subQ5,subQ1,subQ6,subQ7,subQ4,subQ3,subQ2,subQ0])],"isStart":false})})}),makeQuery(id+"F8.opExtrude","SWEPT_FACE",FACE,{"disambiguationData":[OSD([sQuery(id+"F7.wireOp",EDGE,"E67")])]})]});}
            var Q5;
            Q5=makeQuery(id+"F8.boolean.opBoolean","INTERSECT",EDGE,{"disambiguationData":[OD(0.0)],"derivedFrom":[makeQuery(id+"F5.opExtrude","SWEPT_FACE",FACE,{"disambiguationData":[OSD([sQuery(id+"F4.wireOp",EDGE,"E30")])]}),makeQuery(id+"F8.opExtrude","SWEPT_FACE",FACE,{"disambiguationData":[OSD([sQuery(id+"F7.wireOp",EDGE,"E67")])]})]});
            fillet(context, id + "F14", {"entities" : qUnion([Q0, Q1, Q2, Q3, Q4, Q5]), "radius" : 3 * mm, "tangentPropagation" : true, "allowEdgeOverflow" : false});
        }
        {
            var Q0;
            Q0=makeQuery(id+"F1.opExtrude","CAP_EDGE",EDGE,{"disambiguationData":[OSD([sQuery(id+"F0.wireOp",EDGE,"E1.bottom")])],"isStart":false});
            fillet(context, id + "F15", {"entities" : qUnion([Q0]), "radius" : 2 * mm, "tangentPropagation" : true, "allowEdgeOverflow" : false});
        }
        {
            var Q0;
            {var subQ0=sQuery(id+"F0.wireOp",EDGE,"E21.filletArc");var subQ1=sQuery(id+"F0.wireOp",EDGE,"E7");var subQ2=sQuery(id+"F0.wireOp",EDGE,"E6");var subQ3=sQuery(id+"F0.wireOp",EDGE,"E5");var subQ4=sQuery(id+"F0.wireOp",EDGE,"E4");var subQ5=sQuery(id+"F0.wireOp",EDGE,"E22.filletArc");var subQ6=sQuery(id+"F0.wireOp",EDGE,"E1.bottom");var subQ7=sQuery(id+"F0.wireOp",EDGE,"E1.right");var subQ8=sQuery(id+"F0.wireOp",EDGE,"E1.top");var subQ9=sQuery(id+"F0.wireOp",EDGE,"E1.left");var subQ10=sQuery(id+"F0.wireOp",EDGE,"E23.filletArc");var subQ11=sQuery(id+"F0.wireOp",EDGE,"E24.filletArc");Q0=makeQuery(id+"F2.boolean.opBoolean","SPLIT",FACE,{"disambiguationData":[TD([makeQuery(id+"F1.opExtrude","SWEPT_FACE",FACE,{"disambiguationData":[OSD([subQ6])]})])],"derivedFrom":makeQuery(id+"F1.opExtrude","CAP_FACE",FACE,{"disambiguationData":[OSD([subQ6,subQ8,subQ9,subQ7,subQ4,subQ3,subQ2,subQ1,subQ0,subQ5,subQ10,subQ11])],"isStart":true})});}
            var sketch = newSketch(context, id + "F16", { "sketchPlane" : qUnion([Q0])});
            skLineSegment(sketch, "E79", {"start": v(0, 90) * mm, "end": v(0, 120) * mm, "construction": true});
            skArc(sketch, "E80", {"start": v(15, 120) * mm, "mid": v(0, 135) * mm, "end": v(-15, 120) * mm});
            skCircle(sketch, "E81", {"center": v(0, 120) * mm, "radius": 6 * mm});
            skLineSegment(sketch, "E82", {"start": v(-15, 120) * mm, "end": v(-15, 108) * mm});
            skLineSegment(sketch, "E83", {"start": v(-15, 108) * mm, "end": v(-33, 90) * mm});
            skLineSegment(sketch, "E84", {"start": v(15, 120) * mm, "end": v(15, 108) * mm});
            skLineSegment(sketch, "E85", {"start": v(15, 108) * mm, "end": v(33, 90) * mm});
            skLineSegment(sketch, "E86", {"start": v(-80, 0) * mm, "end": v(80, 0) * mm, "construction": true});
            skArc(sketch, "E87.MirrorCS", {"start": v(-15, 120) * mm, "mid": v(0, 135) * mm, "end": v(15, 120) * mm});
            skLineSegment(sketch, "E88.MirrorCS", {"start": v(15, -120) * mm, "end": v(15, -108) * mm});
            skLineSegment(sketch, "E89.MirrorCS", {"start": v(-15, -120) * mm, "end": v(-15, -108) * mm});
            skCircle(sketch, "E90.MirrorC", {"center": v(0, -120) * mm, "radius": 6 * mm});
            skLineSegment(sketch, "E91.MirrorCS", {"start": v(15, -108) * mm, "end": v(33, -90) * mm});
            skArc(sketch, "E92.MirrorCS", {"start": v(15, -120) * mm, "mid": v(0, -135) * mm, "end": v(-15, -120) * mm});
            skLineSegment(sketch, "E93.MirrorCS", {"start": v(-15, -108) * mm, "end": v(-33, -90) * mm});
            skArc(sketch, "E94.MirrorCS", {"start": v(-15, -120) * mm, "mid": v(0, -135) * mm, "end": v(15, -120) * mm});
            skLineSegment(sketch, "E95.MirrorCS", {"start": v(0, -90) * mm, "end": v(0, -120) * mm, "construction": true});
            skLineSegment(sketch, "E96", {"start": v(-33, 90) * mm, "end": v(33, 90) * mm});
            skLineSegment(sketch, "E97", {"start": v(-33, -90) * mm, "end": v(33, -90) * mm});
            skSolve(sketch);
        }
        {
            var Q0;
            {var subQ4=sQuery(id+"F16.wireOp",EDGE,"E96");Q0=makeQuery(id+"F16.imprint","IMPRINT",FACE,{"disambiguationData":[TD([[makeQuery(id+"F16.imprint","IMPRINT",EDGE,{"derivedFrom":subQ4}),-1.0]])]});}
            var Q1;
            Q1=makeQuery(id+"F16.imprint","IMPRINT",FACE,{"disambiguationData":[TD([[makeQuery(id+"F16.imprint","IMPRINT",EDGE,{"derivedFrom":sQuery(id+"F16.wireOp",EDGE,"E89.MirrorCS")}),-1.0]])]});
            var Q2;
            Q2=makeQuery(id+"F16.imprint","IMPRINT",FACE,{"disambiguationData":[TD([[makeQuery(id+"F16.imprint","IMPRINT",EDGE,{"derivedFrom":sQuery(id+"F16.wireOp",EDGE,"E87.MirrorCS")}),-1.0]])]});
            var Q3;
            Q3=makeQuery(id+"F2.opExtrude","CAP_FACE",FACE,{"disambiguationData":[OSD([sQuery(id+"F0.wireOp",EDGE,"E12"),sQuery(id+"F0.wireOp",EDGE,"E13"),sQuery(id+"F0.wireOp",EDGE,"E14"),sQuery(id+"F0.wireOp",EDGE,"E15"),sQuery(id+"F0.wireOp",EDGE,"E17.filletArc"),sQuery(id+"F0.wireOp",EDGE,"E18.filletArc"),sQuery(id+"F0.wireOp",EDGE,"E19.filletArc"),sQuery(id+"F0.wireOp",EDGE,"E20.filletArc"),sQuery(id+"F0.wireOp",EDGE,"E25.0"),sQuery(id+"F0.wireOp",EDGE,"E25.1"),sQuery(id+"F0.wireOp",EDGE,"E25.2"),sQuery(id+"F0.wireOp",EDGE,"E25.3"),sQuery(id+"F0.wireOp",EDGE,"E25.4"),sQuery(id+"F0.wireOp",EDGE,"E25.5"),sQuery(id+"F0.wireOp",EDGE,"E25.6"),sQuery(id+"F0.wireOp",EDGE,"E25.7")])],"isStart":false});
            extrude(context, id + "F17", {"entities" : qUnion([Q0, Q1, Q2]), "endBound" : BoundingType.UP_TO_SURFACE, "endBoundEntityFace" : qUnion([Q3]), "depth" : 25 * mm});
        }
    });
